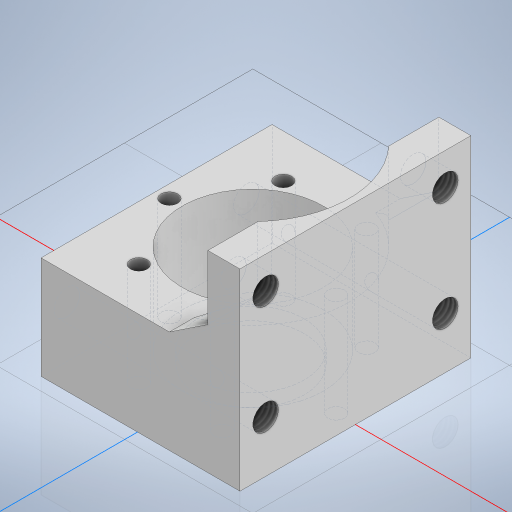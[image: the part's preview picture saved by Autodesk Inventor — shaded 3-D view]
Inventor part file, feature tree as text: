
AUTODESK INVENTOR PART (.ipt)
format: ipt  version: 2024 (Build 280153000, 153)  size: 311,296 bytes
history: native  units: mm
features: extrude x6, sketch x6, thread x4
ambient origin geometry x8: Origin, YZ Plane, XZ Plane, XY Plane, X Axis, Y Axis, Z Axis, Center Point
bodies: Solid1 (feature_tree)
feature tree (16):
  extrude  "Extrusion1"  Depth=15.0mm
  extrude  "Extrusion2"  Depth=18.0mm
  extrude  "Extrusion3"  Depth=30.0mm TaperAngle=0.0deg
  extrude  "Extrusion4"  Depth=30.0mm TaperAngle=0.0deg
  extrude  "Extrusion5"  Depth=2.0mm TaperAngle=0.0deg
  thread  "Thread1"  [1 undecoded]
  thread  "Thread2"  [1 undecoded]
  thread  "Thread3"  [1 undecoded]
  thread  "Thread4"  [1 undecoded]
  extrude  "Extrusion6"  Depth=30.0mm
  sketch  "Sketch1"  dims[d0=22.0mm d1=15.0mm]
  sketch  "Sketch3"  dims[d2=16.0mm d3=18.0mm]
  sketch  "Sketch4"  dims[d4=18.0mm d5=30.0mm d6=0.0mm]
  sketch  "Sketch5"  dims[d7=16.0mm d8=30.0mm d9=0.0mm]
  sketch  "Sketch6"  dims[d10=14.0mm d11=0.0mm d12=2.0mm d13=0.0mm d14=200.0mm d15=0.0mm d16=5.0mm d17=0.0mm d18=5.0mm d19=0.0mm d20=30.0mm d21=0.0mm]
  sketch  "Sketch7"  dims[d22=30.0mm d23=0.0mm d24=30.0mm d25=2.6mm d26=13.0mm d27=60.0mm d29=360.0deg d31=200.0mm d32=0.0mm]
note: 4 required parameter values undecoded (feature->parameter linkage not recoverable at this tier; creation-order binding heuristic only, values carry confidence <= 0.55)
